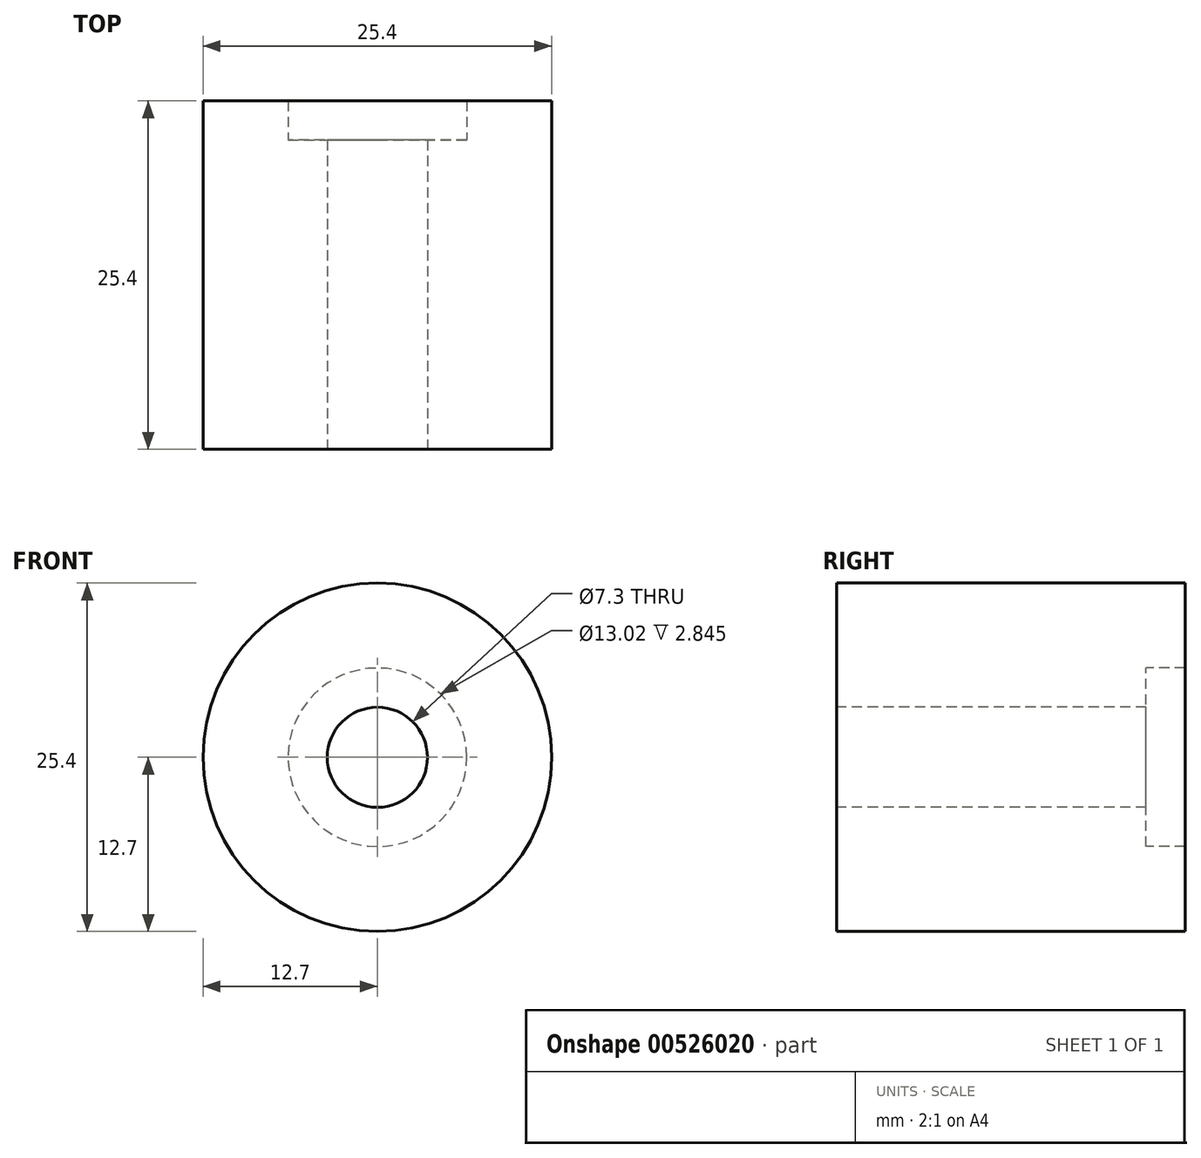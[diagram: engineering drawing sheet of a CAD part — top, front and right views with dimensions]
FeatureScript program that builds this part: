
annotation { "Feature Type Name" : "Feature", "Feature Type Description" : "" }
export const myFeature = defineFeature(function(context is Context, id is Id, definition is map)
    precondition{}
    {
        {
            var Q0;
            Q0=qCreatedBy(makeId("Front.planeOp"),FACE);
            var sketch = newSketch(context, id + "F0", { "sketchPlane" : qUnion([Q0])});
            skCircle(sketch, "E0", {"center": v(0, 0) * mm, "radius": 12.7 * mm});
            skPoint(sketch, "E1", {"position": v(0, -6.79) * mm});
            skSolve(sketch);
        }
        {
            var Q0;
            Q0 = qSketchRegion(id + "F0", true);
            extrude(context, id + "F1", {"entities" : qUnion([Q0]), "depth" : 25.4 * mm, "offsetDistance" : 25.4 * mm});
        }
        {
            var Q0;
            Q0=sQuery(id+"F0.wireOp",VERTEX,"E0.center");
            var Q1;
            Q1=makeQuery(id+"F1.opExtrude","SWEPT_BODY",BODY,{"disambiguationData":[OSD([sQuery(id+"F0.wireOp",EDGE,"E0")])]});
            hole(context, id + "F2", {"style" : HoleStyle.C_BORE, "endStyle" : HoleEndStyle.THROUGH, "oppositeDirection" : true, "holeDiameter" : 7.3 * mm, "cBoreDiameter" : 13.02 * mm, "cBoreDepth" : 2.84 * mm, "majorDiameter" : 6.35 * mm, "tappedDepth" : 12.7 * mm, "tapClearance" : 3, "startFromSketch" : true, "locations" : qUnion([Q0]), "scope" : qUnion([Q1])});
        }
    });
